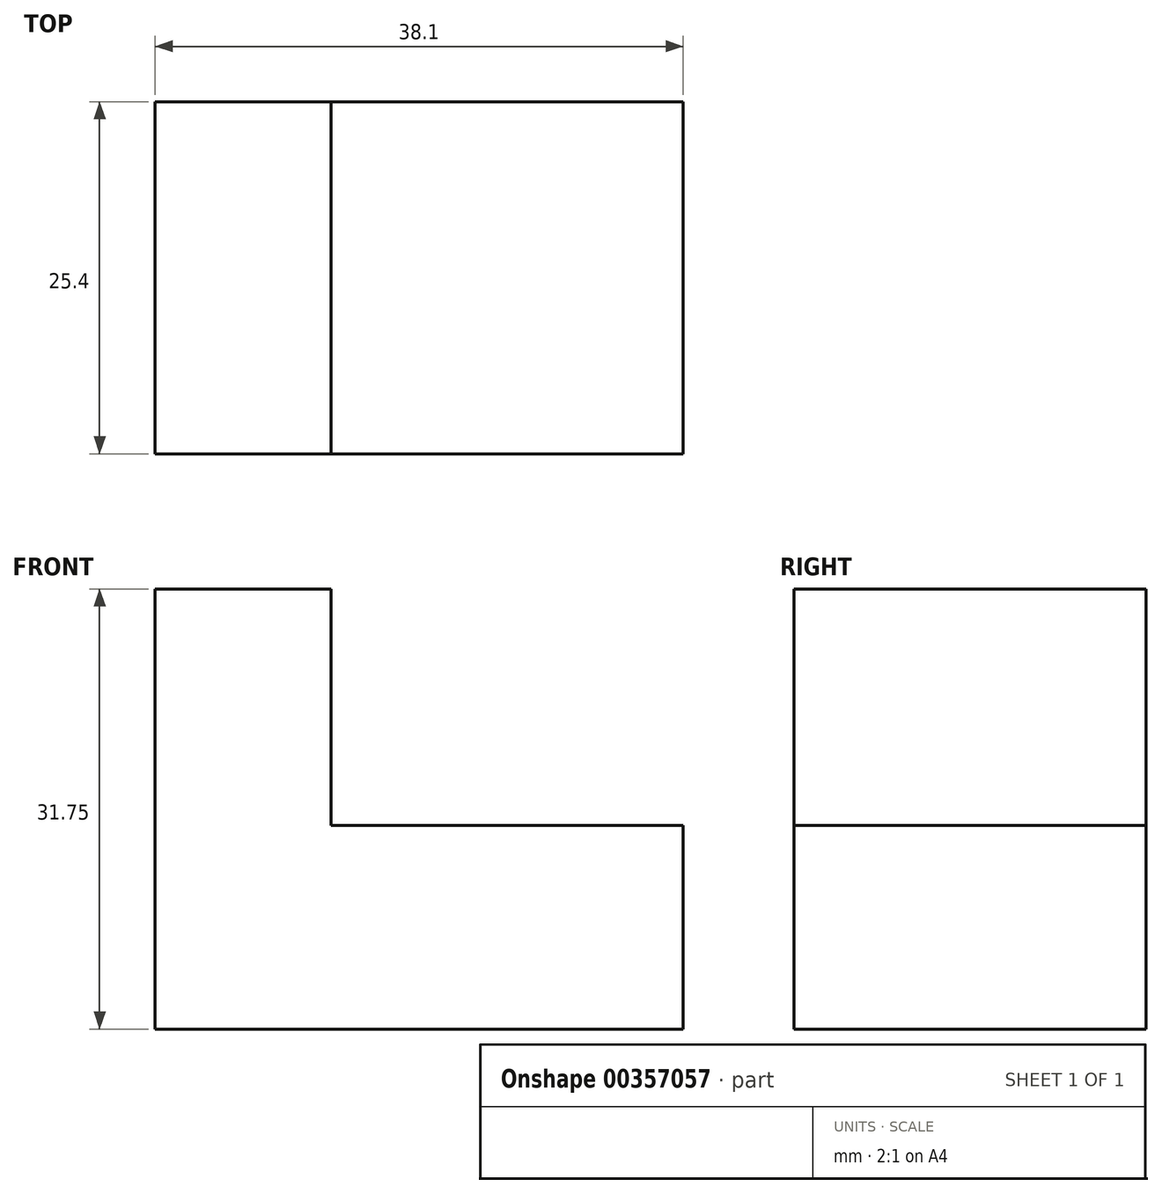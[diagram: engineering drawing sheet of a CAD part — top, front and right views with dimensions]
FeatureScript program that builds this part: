
annotation { "Feature Type Name" : "Feature", "Feature Type Description" : "" }
export const myFeature = defineFeature(function(context is Context, id is Id, definition is map)
    precondition{}
    {
        {
            var Q0;
            Q0=qCreatedBy(makeId("Front.planeOp"),FACE);
            var sketch = newSketch(context, id + "F0", { "sketchPlane" : qUnion([Q0])});
            skLineSegment(sketch, "E0", {"start": v(0, 0) * mm, "end": v(38.1, 0) * mm});
            skLineSegment(sketch, "E1", {"start": v(38.1, 0) * mm, "end": v(38.1, 14.68) * mm});
            skLineSegment(sketch, "E2", {"start": v(38.1, 14.68) * mm, "end": v(12.7, 14.68) * mm});
            skLineSegment(sketch, "E3", {"start": v(12.7, 14.68) * mm, "end": v(12.7, 31.75) * mm});
            skLineSegment(sketch, "E4", {"start": v(12.7, 31.75) * mm, "end": v(0, 31.75) * mm});
            skLineSegment(sketch, "E5", {"start": v(0, 31.75) * mm, "end": v(0, 0) * mm});
            skSolve(sketch);
        }
        {
            var Q0;
            Q0 = qSketchRegion(id + "F0", true);
            extrude(context, id + "F1", {"entities" : qUnion([Q0]), "depth" : 25.4 * mm});
        }
    });
